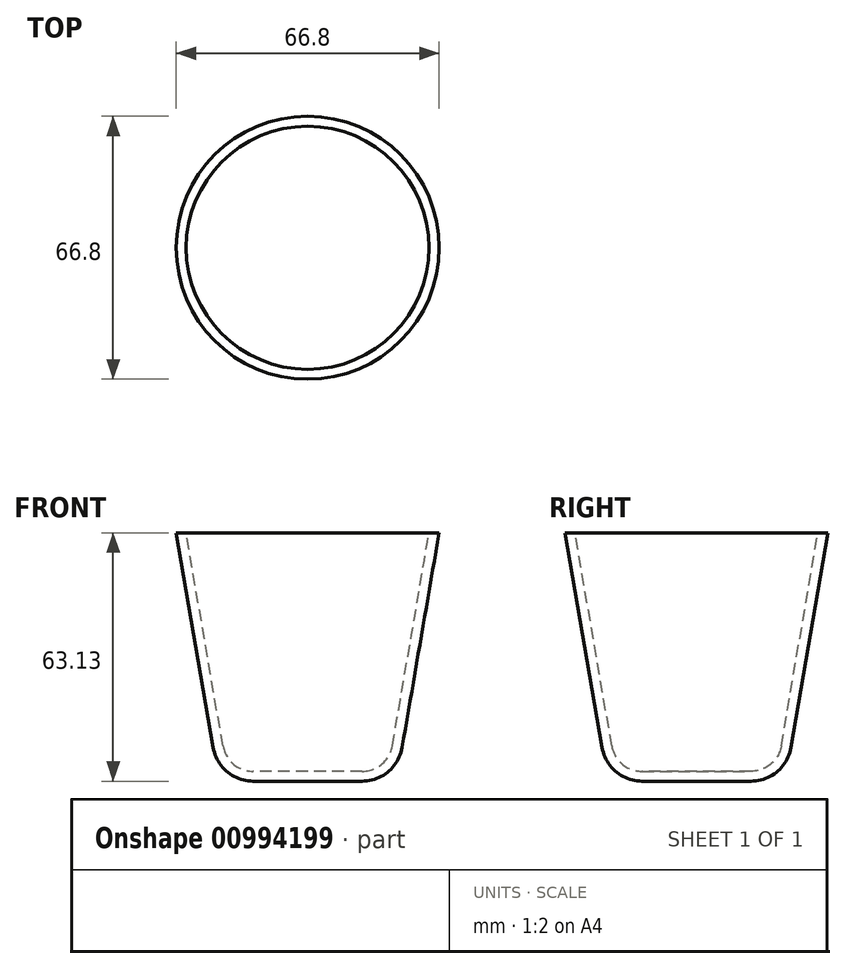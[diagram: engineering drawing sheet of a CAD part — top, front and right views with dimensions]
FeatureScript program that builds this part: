
annotation { "Feature Type Name" : "Feature", "Feature Type Description" : "" }
export const myFeature = defineFeature(function(context is Context, id is Id, definition is map)
    precondition{}
    {
        {
            var Q0;
            Q0=qCreatedBy(makeId("Front.planeOp"),FACE);
            var sketch = newSketch(context, id + "F0", { "sketchPlane" : qUnion([Q0])});
            skLineSegment(sketch, "E0", {"start": v(23.99, 8.54) * mm, "end": v(33.4, 63.13) * mm});
            skLineSegment(sketch, "E1", {"start": v(33.4, 63.13) * mm, "end": v(0, 63.13) * mm});
            skLineSegment(sketch, "E2", {"start": v(0, 63.13) * mm, "end": v(0, 0) * mm});
            skLineSegment(sketch, "E3", {"start": v(0, 0) * mm, "end": v(13.85, 0) * mm});
            skArc(sketch, "E4", {"start": v(13.85, 0) * mm, "mid": v(20.48, 2.42) * mm, "end": v(23.99, 8.54) * mm});
            skLineSegment(sketch, "E5", {"start": v(0, 74.25) * mm, "end": v(0, -12.5) * mm, "construction": true});
            skSolve(sketch);
        }
        {
            var Q0;
            Q0=makeQuery(id+"F0.imprint","IMPRINT",FACE,{"disambiguationData":[TD([[makeQuery(id+"F0.imprint","IMPRINT",EDGE,{"derivedFrom":sQuery(id+"F0.wireOp",EDGE,"E0")}),1.0]])]});
            var Q1;
            Q1=sQuery(id+"F0.wireOp",EDGE,"E5");
            revolve(context, id + "F1", {"surfaceOperationType" : NewSurfaceOperationType.NEW, "entities" : qUnion([Q0]), "axis" : qUnion([Q1]), "revolveType" : RevolveType.FULL});
        }
        {
            var Q0;
            Q0=makeQuery(id+"F1.opRevolve","SWEPT_FACE",FACE,{"disambiguationData":[OSD([sQuery(id+"F0.wireOp",EDGE,"E1")])]});
            shell(context, id + "F2", {"entities" : qUnion([Q0]), "thickness" : 2.5 * mm});
        }
        {
            var Q0;
            Q0=qCreatedBy(makeId("Front.planeOp"),FACE);
            var sketch = newSketch(context, id + "F3", { "sketchPlane" : qUnion([Q0])});
            skArc(sketch, "E6", {"start": v(31.58, 50.75) * mm, "mid": v(45.1, 49.07) * mm, "end": v(44.32, 35.47) * mm});
            skLineSegment(sketch, "E7", {"start": v(25.37, 17.4) * mm, "end": v(44.32, 35.47) * mm});
            skSolve(sketch);
        }
        {
            var Q0;
            Q0=qCreatedBy(makeId("Top.planeOp"),FACE);
            var sketch = newSketch(context, id + "F4", { "sketchPlane" : qUnion([Q0])});
            skCircle(sketch, "E8", {"center": v(58.82, 16.74) * mm, "radius": 2.5 * mm});
            skSolve(sketch);
        }
        {
            var Q0;
            Q0=makeQuery(id+"F4.imprint","IMPRINT",FACE,{"disambiguationData":[TD([[makeQuery(id+"F4.imprint","IMPRINT",EDGE,{"derivedFrom":sQuery(id+"F4.wireOp",EDGE,"E8")}),1.0]])]});
            var Q1;
            Q1=sQuery(id+"F3.wireOp",EDGE,"E7");
            var Q2;
            Q2=sQuery(id+"F3.wireOp",EDGE,"E6");
            sweep(context, id + "F5", {"profiles" : qUnion([Q0]), "path" : qUnion([Q1, Q2])});
        }
        {
            var Q0;
            Q0=makeQuery(id+"F5.opSweep","SWEPT_BODY",BODY,{"disambiguationData":[OSD([sQuery(id+"F3.wireOp",EDGE,"E6"),sQuery(id+"F4.wireOp",EDGE,"E8")])]});
            deleteBodies(context, id + "F6", {"entities" : qUnion([Q0])});
        }
    });
